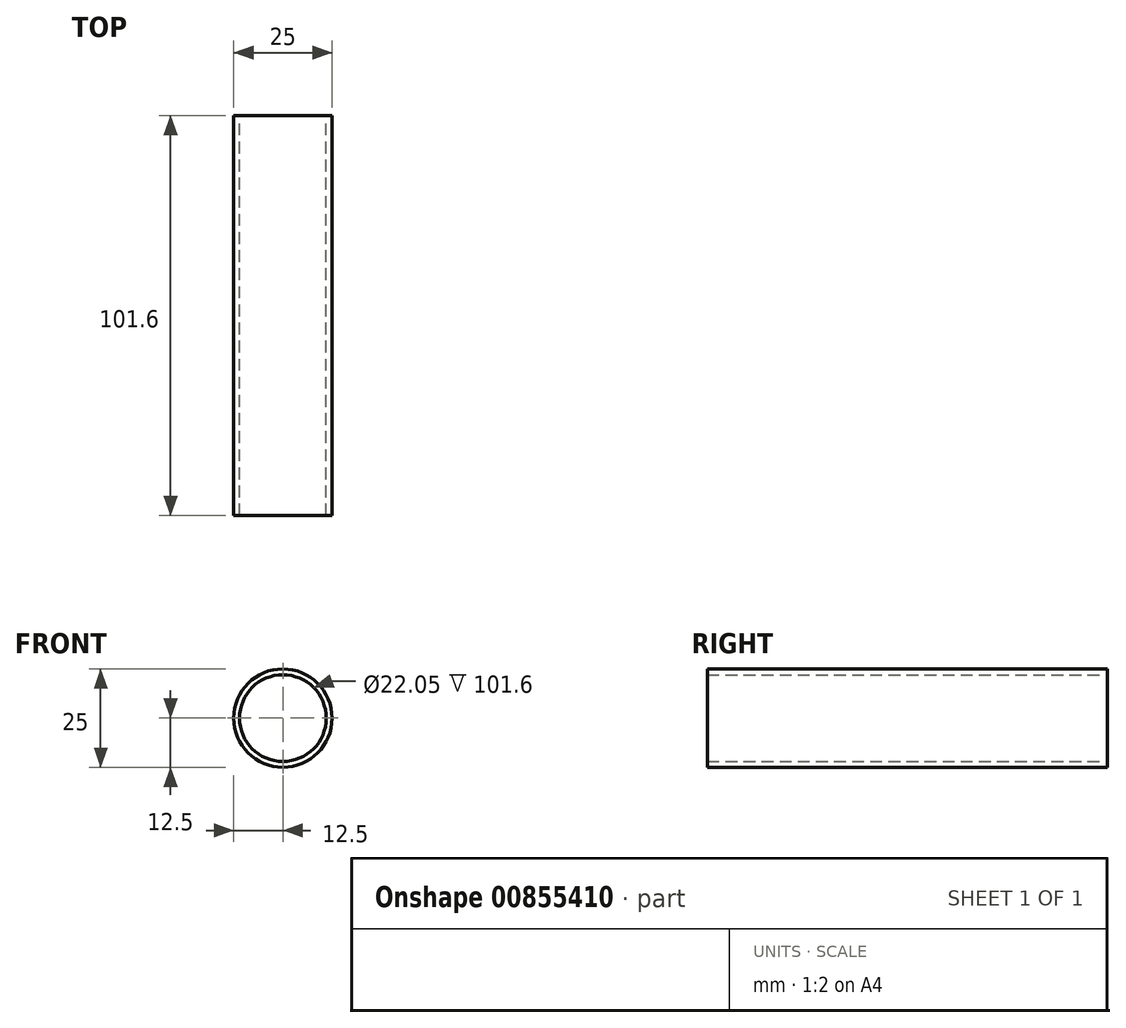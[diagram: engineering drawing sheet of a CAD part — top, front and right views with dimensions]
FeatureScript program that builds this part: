
annotation { "Feature Type Name" : "Feature", "Feature Type Description" : "" }
export const myFeature = defineFeature(function(context is Context, id is Id, definition is map)
    precondition{}
    {
        {
            var Q0;
            Q0=qCreatedBy(makeId("Front.planeOp"),FACE);
            var sketch = newSketch(context, id + "F0", { "sketchPlane" : qUnion([Q0])});
            skCircle(sketch, "E0", {"center": v(0, 0) * mm, "radius": 12.5 * mm});
            skSolve(sketch);
        }
        {
            var Q0;
            Q0 = qSketchRegion(id + "F0", true);
            extrude(context, id + "F1", {"entities" : qUnion([Q0]), "depth" : 101.6 * mm, "offsetDistance" : 25.4 * mm});
        }
        {
            var Q0;
            Q0 = qSketchRegion(id + "F0", true);
            extrude(context, id + "F2", {"entities" : qUnion([Q0]), "operationType" : NewBodyOperationType.ADD, "depth" : 25.4 * mm, "offsetDistance" : 25.4 * mm});
        }
        {
            var Q0;
            Q0=makeQuery(id+"F1.opExtrude","CAP_FACE",FACE,{"disambiguationData":[OSD([sQuery(id+"F0.wireOp",EDGE,"E0")])],"isStart":true});
            var sketch = newSketch(context, id + "F3", { "sketchPlane" : qUnion([Q0])});
            skCircle(sketch, "E1", {"center": v(0, 0) * mm, "radius": 11.03 * mm});
            skSolve(sketch);
        }
        {
            var Q0;
            Q0=makeQuery(id+"F3.imprint","IMPRINT",FACE,{"disambiguationData":[TD([[makeQuery(id+"F3.imprint","IMPRINT",EDGE,{"derivedFrom":sQuery(id+"F3.wireOp",EDGE,"E1")}),1.0]])]});
            extrude(context, id + "F4", {"entities" : qUnion([Q0]), "operationType" : NewBodyOperationType.REMOVE, "oppositeDirection" : true, "depth" : 291.08 * mm, "offsetDistance" : 25.4 * mm});
        }
    });
